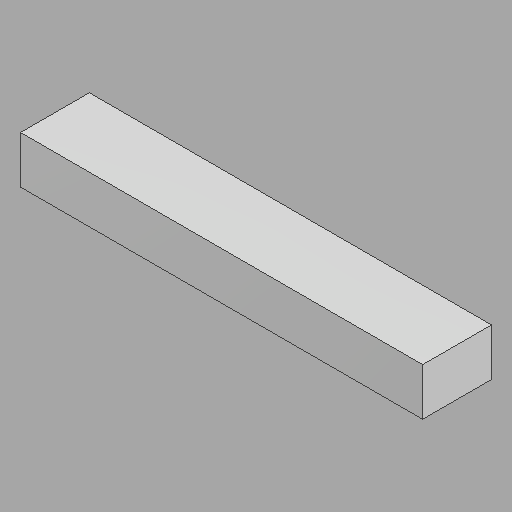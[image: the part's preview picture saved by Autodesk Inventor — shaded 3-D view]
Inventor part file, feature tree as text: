
AUTODESK INVENTOR PART (.ipt)
format: ipt  version: 2022.2 (Build 262287010, 287A)  size: 114,176 bytes
history: native  units: in
note: dims shown in document units (in); Inventor stores cm internally (conversion verified against a paired STEP export)
features: direct_edit x1, other x1, revolve x1
ambient origin geometry x8: Origin, YZ Plane, XZ Plane, XY Plane, X Axis, Y Axis, Z Axis, Center Point
bodies: Solid1 (feature_tree)
feature tree (3):
  direct_edit  "Direct Edit1"
  other  "L Vert rect jamb upper (1)"
  revolve  "Rotate1"  Angle=90.0deg
